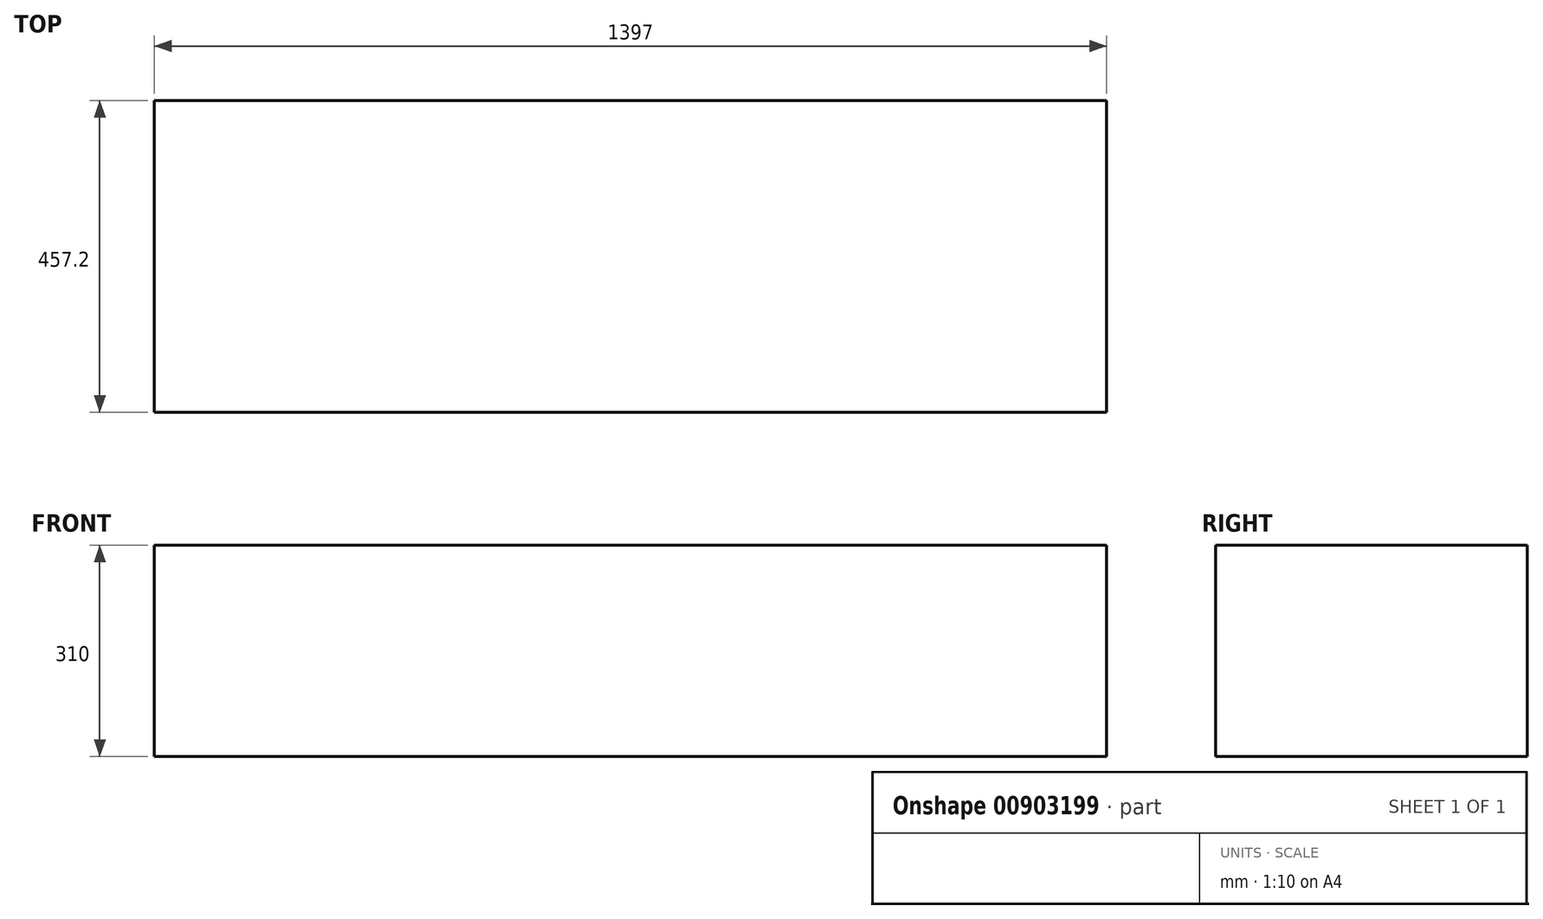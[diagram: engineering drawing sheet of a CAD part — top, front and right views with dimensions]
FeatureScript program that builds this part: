
annotation { "Feature Type Name" : "Feature", "Feature Type Description" : "" }
export const myFeature = defineFeature(function(context is Context, id is Id, definition is map)
    precondition{}
    {
        {
            var Q0;
            Q0=qCreatedBy(makeId("Top.planeOp"),FACE);
            var sketch = newSketch(context, id + "F0", { "sketchPlane" : qUnion([Q0])});
            skLineSegment(sketch, "E0.bottom", {"start": v(698.5, 228.6) * mm, "end": v(-698.5, 228.6) * mm});
            skLineSegment(sketch, "E0.top", {"start": v(698.5, -228.6) * mm, "end": v(-698.5, -228.6) * mm});
            skLineSegment(sketch, "E0.left", {"start": v(698.5, 228.6) * mm, "end": v(698.5, -228.6) * mm});
            skLineSegment(sketch, "E0.right", {"start": v(-698.5, 228.6) * mm, "end": v(-698.5, -228.6) * mm});
            skPoint(sketch, "E0.middle", {"position": v(0, 0) * mm});
            skSolve(sketch);
        }
        {
            var Q0;
            Q0=makeQuery(id+"F0.imprint","IMPRINT",FACE,{"disambiguationData":[TD([[makeQuery(id+"F0.imprint","IMPRINT",EDGE,{"derivedFrom":sQuery(id+"F0.wireOp",EDGE,"9rpZZJUd-G0Hs-47cn-PlUB-uehpF1tbDpLK")}),1.0]])]});
            var Q1;
            Q1=makeQuery(id+"F0.imprint","IMPRINT",FACE,{"disambiguationData":[TD([[makeQuery(id+"F0.imprint","IMPRINT",EDGE,{"derivedFrom":sQuery(id+"F0.wireOp",EDGE,"E0.bottom")}),1.0]])]});
            extrude(context, id + "F1", {"entities" : qUnion([Q0, Q1]), "depth" : 310 * mm, "offsetDistance" : 25.4 * mm});
        }
    });
